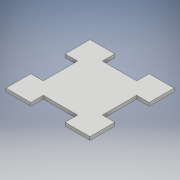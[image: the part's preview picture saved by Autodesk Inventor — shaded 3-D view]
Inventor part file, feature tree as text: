
AUTODESK INVENTOR PART (.ipt)
format: ipt  version: 2018 (Build 220112000, 112)  size: 123,904 bytes
history: native  units: mm
features: other x1, extrude x1, sketch x1
ambient origin geometry x8: Origin, YZ Plane, XZ Plane, XY Plane, X Axis, Y Axis, Z Axis, Center Point
bodies: Body1 (feature_tree)
feature tree (3):
  other  "Bryła1"
  extrude  "Wyciągnięcie proste1"  Depth=152.0mm
  sketch  "Szkic1"
